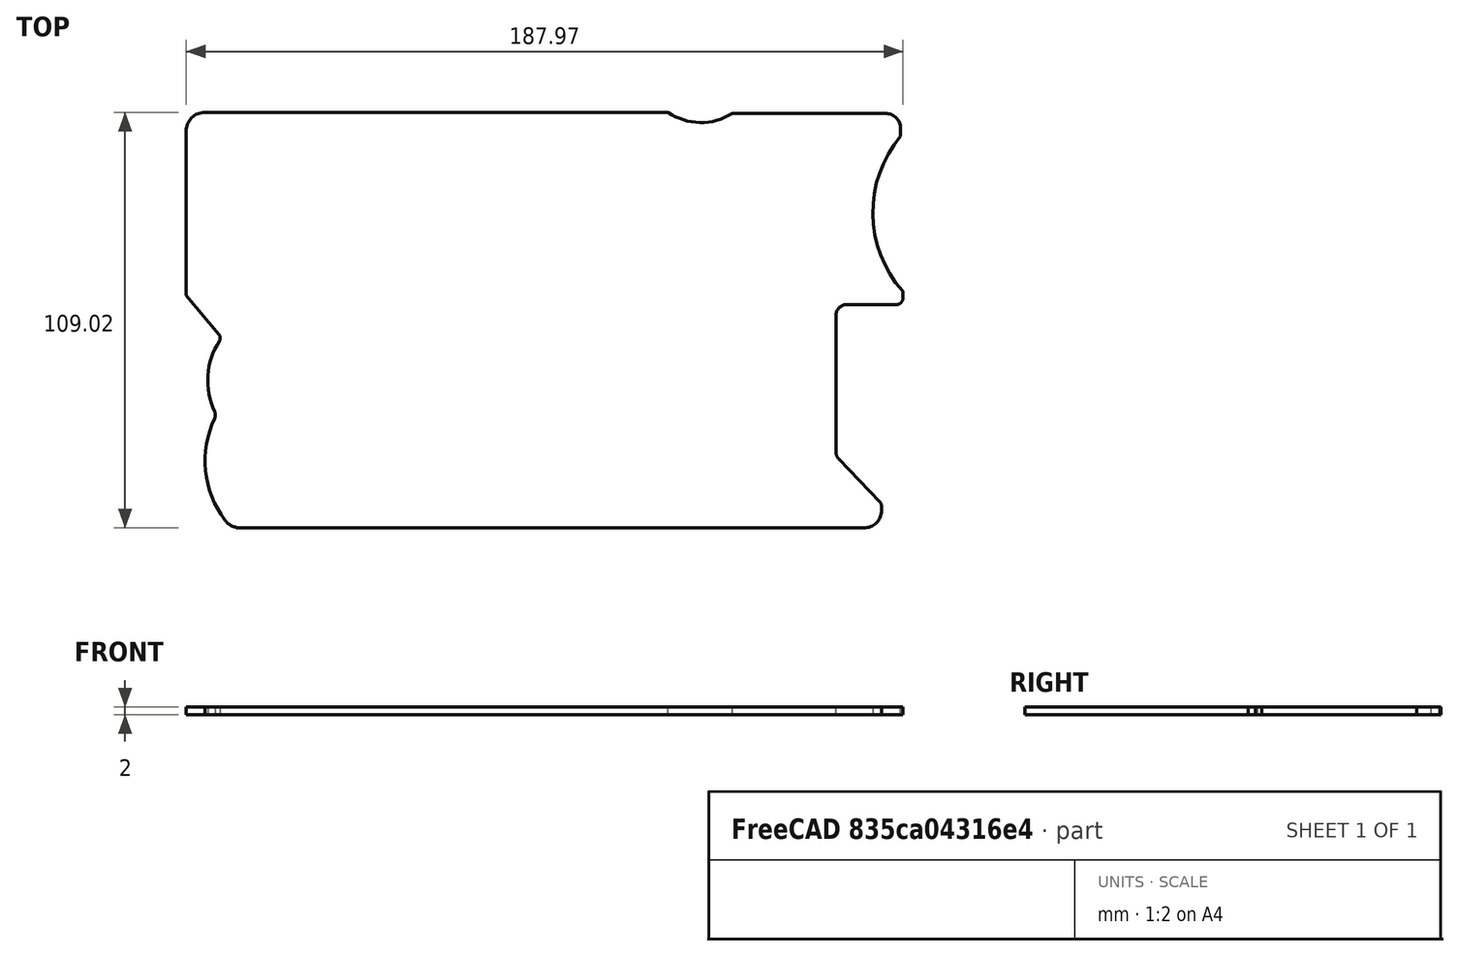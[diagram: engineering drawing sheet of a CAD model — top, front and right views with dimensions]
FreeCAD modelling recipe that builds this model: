
FCSTD DOCUMENT  (FreeCAD 0.20R29177 (Git))
Label: PCB design shape
License: All rights reserved
LicenseURL: http://en.wikipedia.org/wiki/All_rights_reserved
objects: Mesh::Feature×3, Sketcher::SketchObject×2, PartDesign::Body×2, PartDesign::Pad×1, PartDesign::FeatureBase×1
note: 7 computed .brp shape members not serialized (recipe doc carries the construction recipe); baked Part::Feature solids carry a one-line shape summary decoded from their .brp

FEATURE [Mesh::Feature] Base
FEATURE [Mesh::Feature] Cover
  Placement = pos=(0,0,91) rot=(0,0,1;0rad)
FEATURE [Mesh::Feature] Letters
  Placement = pos=(250,0,15) rot=(0,0,1;0rad)
FEATURE [Sketcher::SketchObject] Sketch
  FullyConstrained = false
  MapMode = 5
  Support = -> [XY_Plane]
  sketch-geometry (25):
    g0: LineSegment StartX=410.984 StartY=54.7283 StartZ=0 EndX=532.426 EndY=54.7283 EndZ=0
    g1: LineSegment StartX=593.446 StartY=50.4504 StartZ=0 EndX=593.446 EndY=48.4179 EndZ=0
    g2: LineSegment StartX=583.804 StartY=-54.2856 StartZ=0 EndX=420.385 EndY=-54.2856 EndZ=0
    g3: LineSegment StartX=406.097 StartY=6.73396 StartZ=0 EndX=406.097 EndY=49.8407 EndZ=0
    g4: ArcOfCircle CenterX=541.082 CenterY=67.307 CenterZ=0 NormalX=0 NormalY=0 NormalZ=1 AngleXU=0 Radius=15.2692 StartAngle=4.10966 EndAngle=5.28376
    g5: ArcOfCircle CenterX=617.189 CenterY=28.4278 CenterZ=0 NormalX=0 NormalY=0 NormalZ=1 AngleXU=0 Radius=31.0375 StartAngle=2.44179 EndAngle=3.86807
    g6: LineSegment StartX=579.288 StartY=4.28428 StartZ=0 EndX=592.266 EndY=4.28428 EndZ=0
    g7: LineSegment StartX=576.473 StartY=-34.3297 StartZ=0 EndX=576.473 EndY=1.46836 EndZ=0
    g8: LineSegment StartX=577.24 StartY=-36.2436 StartZ=0 EndX=587.951 EndY=-47.4535 EndZ=0
    g9: LineSegment StartX=588.479 StartY=-48.8004 StartZ=0 EndX=588.466 EndY=-49.6909 EndZ=0
    g10: LineSegment StartX=406.097 StartY=6.73396 StartZ=0 EndX=414.682 EndY=-3.55576 EndZ=0
    g11: ArcOfCircle CenterX=430.76 CenterY=-15.6382 CenterZ=0 NormalX=0 NormalY=0 NormalZ=1 AngleXU=0 Radius=19.0343 StartAngle=2.56663 EndAngle=3.58067
    g12: ArcOfCircle CenterX=437.062 CenterY=-36.6652 CenterZ=0 NormalX=0 NormalY=0 NormalZ=1 AngleXU=0 Radius=26.0034 StartAngle=2.70203 EndAngle=3.78081
    g13: ArcOfCircle CenterX=589.433 CenterY=50.4504 CenterZ=0 NormalX=0 NormalY=0 NormalZ=1 AngleXU=0 Radius=4.01265 StartAngle=-9e-16 EndAngle=1.56794
    g14: ArcOfCircle CenterX=592.266 CenterY=6.08736 CenterZ=0 NormalX=0 NormalY=0 NormalZ=1 AngleXU=0 Radius=1.80308 StartAngle=4.71239 EndAngle=6.28362
    g15: LineSegment StartX=593.987 StartY=7.8114 StartZ=0 EndX=594.069 EndY=6.08814 EndZ=0
    g16: LineSegment StartX=549.34 StartY=54.4631 StartZ=0 EndX=589.445 EndY=54.4631 EndZ=0
    g17: ArcOfCircle CenterX=579.288 CenterY=1.46836 CenterZ=0 NormalX=0 NormalY=0 NormalZ=1 AngleXU=0 Radius=2.81593 StartAngle=1.5708 EndAngle=3.14159
    g18: ArcOfCircle CenterX=583.804 CenterY=-49.623 CenterZ=0 NormalX=0 NormalY=0 NormalZ=1 AngleXU=0 Radius=4.66258 StartAngle=4.71239 EndAngle=6.26864
    g19: ArcOfCircle CenterX=586.57 CenterY=-48.7726 CenterZ=0 NormalX=0 NormalY=0 NormalZ=1 AngleXU=0 Radius=1.90944 StartAngle=6.26864 EndAngle=7.04582
    g20: ArcOfCircle CenterX=420.385 CenterY=-49.0616 CenterZ=0 NormalX=0 NormalY=0 NormalZ=1 AngleXU=0 Radius=5.22406 StartAngle=3.78081 EndAngle=4.71239
    g21: ArcOfCircle CenterX=413.559 CenterY=-4.49227 CenterZ=0 NormalX=0 NormalY=0 NormalZ=1 AngleXU=0 Radius=1.46186 StartAngle=5.70822 EndAngle=6.9785
    g22: ArcOfCircle CenterX=411.541 CenterY=-24.6643 CenterZ=0 NormalX=0 NormalY=0 NormalZ=1 AngleXU=0 Radius=2.19816 StartAngle=5.84362 EndAngle=6.72227
    g23: ArcOfCircle CenterX=579.243 CenterY=-34.3297 CenterZ=0 NormalX=0 NormalY=0 NormalZ=1 AngleXU=0 Radius=2.7704 StartAngle=3.14159 EndAngle=3.90422
    g24: ArcOfCircle CenterX=410.984 CenterY=49.8407 CenterZ=0 NormalX=0 NormalY=0 NormalZ=1 AngleXU=0 Radius=4.88762 StartAngle=1.5708 EndAngle=3.14159
  constraints (32):
    c: Horizontal(g0)
    c: Horizontal(g2)
    c: Vertical(g1)
    c: Vertical(g3)
    c: Horizontal(g6)
    c: Vertical(g7)
    c: Coincident(g16,g13) = 1.5708
    c: Tangent(g1,g13) = 1.5708
    c: Coincident(g15,g14) = 1.5708
    c: Tangent(g6,g14) = -1.5708
    c: Coincident(g1,g5)
    c: Coincident(g15,g5)
    c: Coincident(g0,g4)
    c: Coincident(g16,g4)
    c: Coincident(g3,g10)
    c: Tangent(g6,g17) = 1.5708
    c: Tangent(g7,g17) = 1.5708
    c: Tangent(g2,g18) = 1.5708
    c: Tangent(g9,g18) = 1.5708
    c: Tangent(g8,g19) = 1.5708
    c: Tangent(g9,g19) = 1.5708
    c: Tangent(g2,g20) = 1.5708
    c: Tangent(g12,g20) = -1.5708
    c: Tangent(g10,g21) = 1.5708
    c: Tangent(g11,g21) = 1.5708
    c: Tangent(g11,g22) = 1.5708
    c: Tangent(g12,g22) = 1.5708
    c: Tangent(g8,g23) = -1.5708
    c: Tangent(g7,g23) = 1.5708
    c: Tangent(g0,g24) = 1.5708
    c: Tangent(g3,g24) = 1.5708
    c: Horizontal(g16)
FEATURE [PartDesign::Pad] Pad
  Direction = (0,0,1)
  Length = 2
  Length2 = 10
  Profile = -> Sketch
  ReferenceAxis = -> Sketch [N_Axis]
  Refine = true
  Type = 0
FEATURE [PartDesign::Body] Body  label="PCB"
  Group = -> [Sketch,Pad]
  Origin = -> Origin
  Tip = -> Pad
FEATURE [PartDesign::Body] Body002
  Origin = -> Origin002
FEATURE [PartDesign::FeatureBase] BaseFeature
FEATURE [Sketcher::SketchObject] Sketch001  label="SketchLetters"
  FullyConstrained = false
  MapMode = 5
  sketch-geometry (139):
    g0: LineSegment StartX=405.546 StartY=54.2279 StartZ=0 EndX=416.615 EndY=54.2279 EndZ=0
    g1: LineSegment StartX=422.952 StartY=31.0582 StartZ=0 EndX=416.615 EndY=54.2279 EndZ=0
    g2: LineSegment StartX=422.952 StartY=54.1639 StartZ=0 EndX=422.952 EndY=31.0582 EndZ=0
    g3: LineSegment StartX=431.208 StartY=54.0359 StartZ=0 EndX=422.952 EndY=54.1639 EndZ=0
    g4: LineSegment StartX=431.208 StartY=3.85615 StartZ=0 EndX=431.208 EndY=54.0359 EndZ=0
    g5: LineSegment StartX=421.992 StartY=3.85615 StartZ=0 EndX=431.208 EndY=3.85615 EndZ=0
    g6: LineSegment StartX=414.055 StartY=33.2983 StartZ=0 EndX=421.992 EndY=3.85615 EndZ=0
    g7: LineSegment StartX=414.055 StartY=3.85615 StartZ=0 EndX=414.055 EndY=33.2983 EndZ=0
    g8: LineSegment StartX=405.546 StartY=3.81092 StartZ=0 EndX=414.055 EndY=3.85615 EndZ=0
    g9: LineSegment StartX=405.546 StartY=54.2279 StartZ=0 EndX=405.546 EndY=3.81092 EndZ=0
    g10: GeomPoint X=438.871 Y=54.184 Z=0
    g11: GeomPoint X=461.31 Y=54.184 Z=0
    g12: GeomPoint X=461.31 Y=45.5904 Z=0
    g13: LineSegment StartX=438.871 StartY=54.184 StartZ=0 EndX=461.31 EndY=54.184 EndZ=0
    g14: LineSegment StartX=461.31 StartY=45.5904 StartZ=0 EndX=461.31 EndY=54.184 EndZ=0
    g15: LineSegment StartX=438.871 StartY=54.184 StartZ=0 EndX=438.871 EndY=3.87505 EndZ=0
    g16: LineSegment StartX=461.184 StartY=3.87505 StartZ=0 EndX=438.871 EndY=3.87505 EndZ=0
    g17: LineSegment StartX=461.184 StartY=12.5525 StartZ=0 EndX=461.184 EndY=3.87505 EndZ=0
    g18: LineSegment StartX=461.184 StartY=12.5525 StartZ=0 EndX=448.129 EndY=12.5525 EndZ=0
    g19: LineSegment StartX=448.129 StartY=12.5525 StartZ=0 EndX=448.129 EndY=25.686 EndZ=0
    g20: LineSegment StartX=448.129 StartY=25.686 StartZ=0 EndX=458.682 EndY=25.686 EndZ=0
    g21: LineSegment StartX=458.682 StartY=34.5198 StartZ=0 EndX=458.682 EndY=25.686 EndZ=0
    g22: LineSegment StartX=458.682 StartY=34.5198 StartZ=0 EndX=448.135 EndY=34.5198 EndZ=0
    g23: LineSegment StartX=448.135 StartY=34.5198 StartZ=0 EndX=448.135 EndY=45.5904 EndZ=0
    g24: LineSegment StartX=461.31 StartY=45.5904 StartZ=0 EndX=448.135 EndY=45.5904 EndZ=0
    g25: LineSegment StartX=465.562 StartY=53.9856 StartZ=0 EndX=465.562 EndY=45.5426 EndZ=0
    g26: LineSegment StartX=473.536 StartY=45.5426 StartZ=0 EndX=465.562 EndY=45.5426 EndZ=0
    g27: LineSegment StartX=473.536 StartY=3.7187 StartZ=0 EndX=473.536 EndY=45.5426 EndZ=0
    g28: LineSegment StartX=482.76 StartY=3.7187 StartZ=0 EndX=473.536 EndY=3.7187 EndZ=0
    g29: LineSegment StartX=482.76 StartY=3.7187 StartZ=0 EndX=482.76 EndY=45.5426 EndZ=0
    g30: LineSegment StartX=490.969 StartY=45.5426 StartZ=0 EndX=482.76 EndY=45.5426 EndZ=0
    g31: LineSegment StartX=490.969 StartY=45.5426 StartZ=0 EndX=490.969 EndY=53.9856 EndZ=0
    g32: LineSegment StartX=490.969 StartY=53.9856 StartZ=0 EndX=465.562 EndY=53.9856 EndZ=0
    g33: LineSegment StartX=496.41 StartY=54.2073 StartZ=0 EndX=496.41 EndY=3.71827 EndZ=0
    g34: LineSegment StartX=496.41 StartY=3.71827 StartZ=0 EndX=505.869 EndY=3.71827 EndZ=0
    g35: LineSegment StartX=505.869 StartY=3.71827 StartZ=0 EndX=505.869 EndY=25.0602 EndZ=0
    g36: LineSegment StartX=505.869 StartY=25.0602 StartZ=0 EndX=515.484 EndY=25.0602 EndZ=0
    g37: LineSegment StartX=515.484 StartY=25.0602 StartZ=0 EndX=515.484 EndY=33.7377 EndZ=0
    g38: LineSegment StartX=515.484 StartY=33.7377 StartZ=0 EndX=505.791 EndY=33.7377 EndZ=0
    g39: LineSegment StartX=505.791 StartY=33.7377 StartZ=0 EndX=505.791 EndY=45.5422 EndZ=0
    g40: LineSegment StartX=505.791 StartY=45.5422 StartZ=0 EndX=518.299 EndY=45.5422 EndZ=0
    g41: LineSegment StartX=518.299 StartY=45.5422 StartZ=0 EndX=518.299 EndY=54.2073 EndZ=0
    g42: LineSegment StartX=518.299 StartY=54.2073 StartZ=0 EndX=496.41 EndY=54.2073 EndZ=0
    g43: LineSegment StartX=523.843 StartY=54.2108 StartZ=0 EndX=523.843 EndY=3.71104 EndZ=0
    g44: LineSegment StartX=545.605 StartY=3.71104 StartZ=0 EndX=523.843 EndY=3.71104 EndZ=0
    g45: LineSegment StartX=545.605 StartY=3.71104 StartZ=0 EndX=545.605 EndY=12.5437 EndZ=0
    g46: LineSegment StartX=545.605 StartY=12.5437 StartZ=0 EndX=532.996 EndY=12.5437 EndZ=0
    g47: LineSegment StartX=532.996 StartY=12.5437 StartZ=0 EndX=532.996 EndY=54.2108 EndZ=0
    g48: LineSegment StartX=532.996 StartY=54.2108 StartZ=0 EndX=523.843 EndY=54.2108 EndZ=0
    g49: LineSegment StartX=551.266 StartY=54.0824 StartZ=0 EndX=551.266 EndY=3.77469 EndZ=0
    g50: LineSegment StartX=560.354 StartY=3.77469 StartZ=0 EndX=551.266 EndY=3.77469 EndZ=0
    g51: LineSegment StartX=560.354 StartY=3.77469 StartZ=0 EndX=560.354 EndY=54.0824 EndZ=0
    g52: LineSegment StartX=560.354 StartY=54.0824 StartZ=0 EndX=551.266 EndY=54.0824 EndZ=0
    g53: LineSegment StartX=566.179 StartY=54.1464 StartZ=0 EndX=574.896 EndY=29.6968 EndZ=0
    g54: LineSegment StartX=594.341 StartY=54.2104 StartZ=0 EndX=585.585 EndY=29.5688 EndZ=0
    g55: LineSegment StartX=565.731 StartY=3.9027 StartZ=0 EndX=574.896 EndY=29.6968 EndZ=0
    g56: LineSegment StartX=575.78 StartY=54.1464 StartZ=0 EndX=580.593 EndY=40.4496 EndZ=0
    g57: LineSegment StartX=565.731 StartY=3.9027 StartZ=0 EndX=574.563 EndY=3.9027 EndZ=0
    g58: LineSegment StartX=584.996 StartY=3.77469 StartZ=0 EndX=594.725 EndY=3.77469 EndZ=0
    g59: LineSegment StartX=594.341 StartY=54.2104 StartZ=0 EndX=585.508 EndY=54.2104 EndZ=0
    g60: LineSegment StartX=575.78 StartY=54.1464 StartZ=0 EndX=566.179 EndY=54.1464 EndZ=0
    g61: LineSegment StartX=580.593 StartY=40.4496 StartZ=0 EndX=585.508 EndY=54.2104 EndZ=0
    g62: LineSegment StartX=585.585 StartY=29.5688 StartZ=0 EndX=594.725 EndY=3.77469 EndZ=0
    g63: LineSegment StartX=579.825 StartY=18.816 StartZ=0 EndX=584.996 EndY=3.77469 EndZ=0
    g64: LineSegment StartX=579.825 StartY=18.816 StartZ=0 EndX=574.563 EndY=3.9027 EndZ=0
    g65: LineSegment StartX=565.988 StartY=-3.25487 StartZ=0 EndX=575.396 EndY=-3.25487 EndZ=0
    g66: LineSegment StartX=575.396 StartY=-3.25487 StartZ=0 EndX=575.396 EndY=-44.7299 EndZ=0
    g67: LineSegment StartX=575.396 StartY=-44.7299 StartZ=0 EndX=588.005 EndY=-44.7299 EndZ=0
    g68: LineSegment StartX=588.005 StartY=-44.7299 StartZ=0 EndX=588.005 EndY=-53.5626 EndZ=0
    g69: LineSegment StartX=588.005 StartY=-53.5626 StartZ=0 EndX=565.988 EndY=-53.5626 EndZ=0
    g70: LineSegment StartX=565.988 StartY=-53.5626 StartZ=0 EndX=565.988 EndY=-3.25487 EndZ=0
    g71: LineSegment StartX=538.722 StartY=-3.31887 StartZ=0 EndX=538.722 EndY=-53.5626 EndZ=0
    g72: LineSegment StartX=538.722 StartY=-53.5626 StartZ=0 EndX=560.739 EndY=-53.5626 EndZ=0
    g73: LineSegment StartX=560.739 StartY=-53.5626 StartZ=0 EndX=560.739 EndY=-45.05 EndZ=0
    g74: LineSegment StartX=560.739 StartY=-45.05 StartZ=0 EndX=547.874 EndY=-45.05 EndZ=0
    g75: LineSegment StartX=547.874 StartY=-45.05 StartZ=0 EndX=547.874 EndY=-3.31887 EndZ=0
    g76: LineSegment StartX=547.874 StartY=-3.31887 StartZ=0 EndX=538.722 EndY=-3.31887 EndZ=0
    g77: LineSegment StartX=521.859 StartY=-3.32229 StartZ=0 EndX=521.859 EndY=-53.374 EndZ=0
    g78: LineSegment StartX=521.859 StartY=-53.374 StartZ=0 EndX=531.075 EndY=-53.374 EndZ=0
    g79: LineSegment StartX=531.075 StartY=-53.374 StartZ=0 EndX=531.075 EndY=-3.32229 EndZ=0
    g80: LineSegment StartX=531.075 StartY=-3.32229 StartZ=0 EndX=521.859 EndY=-3.32229 EndZ=0
    g81: LineSegment StartX=489.144 StartY=-3.19528 StartZ=0 EndX=489.144 EndY=-53.503 EndZ=0
    g82: LineSegment StartX=489.144 StartY=-53.503 StartZ=0 EndX=498.361 EndY=-53.503 EndZ=0
    g83: LineSegment StartX=498.361 StartY=-53.503 StartZ=0 EndX=498.361 EndY=-31.7414 EndZ=0
    g84: LineSegment StartX=498.361 StartY=-31.7414 StartZ=0 EndX=504.953 EndY=-31.7414 EndZ=0
    g85: LineSegment StartX=504.953 StartY=-31.7414 StartZ=0 EndX=504.953 EndY=-53.439 EndZ=0
    g86: LineSegment StartX=504.953 StartY=-53.439 StartZ=0 EndX=514.17 EndY=-53.439 EndZ=0
    g87: LineSegment StartX=514.17 StartY=-53.439 StartZ=0 EndX=514.17 EndY=-3.13127 EndZ=0
    g88: LineSegment StartX=514.17 StartY=-3.13127 StartZ=0 EndX=504.953 EndY=-3.13127 EndZ=0
    g89: LineSegment StartX=504.953 StartY=-3.13127 StartZ=0 EndX=504.953 EndY=-23.0367 EndZ=0
    g90: LineSegment StartX=504.953 StartY=-23.0367 StartZ=0 EndX=498.297 EndY=-23.0367 EndZ=0
    g91: LineSegment StartX=498.297 StartY=-23.0367 StartZ=0 EndX=498.297 EndY=-3.13127 EndZ=0
    g92: LineSegment StartX=489.144 StartY=-3.19528 StartZ=0 EndX=498.297 EndY=-3.13127 EndZ=0
    g93: LineSegment StartX=482.961 StartY=-21.1688 StartZ=0 EndX=473.794 EndY=-21.1688 EndZ=0
    g94: LineSegment StartX=473.814 StartY=-33.8649 StartZ=0 EndX=482.541 EndY=-33.8649 EndZ=0
    g95: LineSegment StartX=467.941 StartY=-14.0958 StartZ=0 EndX=467.941 EndY=-43.2309 EndZ=0
    g96: LineSegment StartX=473.814 StartY=-42.8558 StartZ=0 EndX=473.814 EndY=-33.8649 EndZ=0
    g97: LineSegment StartX=473.794 StartY=-21.1688 StartZ=0 EndX=473.794 EndY=-13.9212 EndZ=0
    g98: LineSegment StartX=458.751 StartY=-13.0789 StartZ=0 EndX=458.751 EndY=-44.5006 EndZ=0
    g99: LineSegment StartX=482.541 StartY=-33.8649 StartZ=0 EndX=482.541 EndY=-45.2303 EndZ=0
    g100: LineSegment StartX=482.961 StartY=-21.1688 StartZ=0 EndX=482.961 EndY=-13.405 EndZ=0
    g101: ArcOfCircle CenterX=470.871 CenterY=-14.1044 CenterZ=0 NormalX=0 NormalY=0 NormalZ=1 AngleXU=0 Radius=2.92925 StartAngle=0.0625575 EndAngle=3.13866
    g102: ArcOfCircle CenterX=470.84 CenterY=-14.4077 CenterZ=0 NormalX=0 NormalY=0 NormalZ=1 AngleXU=0 Radius=12.1622 StartAngle=0.0825419 EndAngle=3.03211
    g103: ArcOfCircle CenterX=470.854 CenterY=-42.6787 CenterZ=0 NormalX=0 NormalY=0 NormalZ=1 AngleXU=0 Radius=2.96468 StartAngle=3.32895 EndAngle=6.22339
    g104: ArcOfCircle CenterX=470.729 CenterY=-42.1506 CenterZ=0 NormalX=0 NormalY=0 NormalZ=1 AngleXU=0 Radius=12.2064 StartAngle=3.33532 EndAngle=6.02812
    g105: LineSegment StartX=421.459 StartY=-3.29966 StartZ=0 EndX=433.493 EndY=-3.29966 EndZ=0
    g106: LineSegment StartX=436.191 StartY=-17.5919 StartZ=0 EndX=436.191 EndY=-23.0973 EndZ=0
    g107: LineSegment StartX=420.596 StartY=-54.239 StartZ=0 EndX=419.544 EndY=-54.239 EndZ=0
    g108: LineSegment StartX=411.513 StartY=-46.657 StartZ=0 EndX=411.513 EndY=-34.1508 EndZ=0
    g109: LineSegment StartX=438.418 StartY=-23.0973 StartZ=0 EndX=436.191 EndY=-23.0973 EndZ=0
    g110: LineSegment StartX=423.276 StartY=-31.8053 StartZ=0 EndX=426.847 EndY=-31.8053 EndZ=0
    g111: LineSegment StartX=438.418 StartY=-31.6875 StartZ=0 EndX=438.418 EndY=-23.0973 EndZ=0
    g112: LineSegment StartX=426.879 StartY=-17.5919 StartZ=0 EndX=436.191 EndY=-17.5919 EndZ=0
    g113: LineSegment StartX=436.191 StartY=-17.5919 StartZ=0 EndX=436.191 EndY=-23.0973 EndZ=0
    g114: LineSegment StartX=426.847 StartY=-42.5663 StartZ=0 EndX=426.847 EndY=-31.8053 EndZ=0
    g115: LineSegment StartX=433.535 StartY=-11.8134 StartZ=0 EndX=424.319 EndY=-11.8134 EndZ=0
    g116: LineSegment StartX=421.459 StartY=-3.29966 StartZ=0 EndX=433.535 EndY=-3.29966 EndZ=0
    g117: LineSegment StartX=433.535 StartY=-3.29966 StartZ=0 EndX=433.535 EndY=-11.8134 EndZ=0
    g118: LineSegment StartX=412.104 StartY=-13.7869 StartZ=0 EndX=412.104 EndY=-19.7178 EndZ=0
    g119: LineSegment StartX=421.072 StartY=-20.2759 StartZ=0 EndX=421.072 EndY=-14.1912 EndZ=0
    g120: LineSegment StartX=411.513 StartY=-34.3077 StartZ=0 EndX=411.513 EndY=-42.9125 EndZ=0
    g121: LineSegment StartX=420.95 StartY=-42.8622 StartZ=0 EndX=420.95 EndY=-34.7435 EndZ=0
    g122: ArcOfCircle CenterX=423.743 CenterY=-20.373 CenterZ=0 NormalX=0 NormalY=0 NormalZ=1 AngleXU=0 Radius=2.67256 StartAngle=3.10523 EndAngle=4.61644
    g123: ArcOfCircle CenterX=423.742 CenterY=-14.4315 CenterZ=0 NormalX=0 NormalY=0 NormalZ=1 AngleXU=0 Radius=2.68085 StartAngle=1.35387 EndAngle=3.05183
    g124: ArcOfCircle CenterX=422.511 CenterY=-13.6547 CenterZ=0 NormalX=0 NormalY=0 NormalZ=1 AngleXU=0 Radius=10.4084 StartAngle=1.67205 EndAngle=3.15429
    g125: ArcOfCircle CenterX=424.261 CenterY=-34.9743 CenterZ=0 NormalX=0 NormalY=0 NormalZ=1 AngleXU=0 Radius=3.31845 StartAngle=1.87205 EndAngle=3.07199
    g126: ArcOfCircle CenterX=423.893 CenterY=-42.5966 CenterZ=0 NormalX=0 NormalY=0 NormalZ=1 AngleXU=0 Radius=2.95456 StartAngle=3.23162 EndAngle=6.29341
    g127: ArcOfCircle CenterX=420.07 CenterY=-45.6373 CenterZ=0 NormalX=0 NormalY=0 NormalZ=1 AngleXU=0 Radius=8.61771 StartAngle=3.2602 EndAngle=4.77347
    g128: LineSegment StartX=436.159 StartY=-31.6875 StartZ=0 EndX=438.418 EndY=-31.6875 EndZ=0
    g129: LineSegment StartX=426.879 StartY=-23.0333 StartZ=0 EndX=426.879 EndY=-17.5919 EndZ=0
    g130: LineSegment StartX=426.879 StartY=-23.0333 StartZ=0 EndX=423.487 EndY=-23.0333 EndZ=0
    g131: LineSegment StartX=436.159 StartY=-31.6875 StartZ=0 EndX=436.159 EndY=-50.1365 EndZ=0
    g132: ArcOfCircle CenterX=420.041 CenterY=-20.028 CenterZ=0 NormalX=0 NormalY=0 NormalZ=1 AngleXU=0 Radius=7.9434 StartAngle=3.10253 EndAngle=4.21528
    g133: ArcOfCircle CenterX=419.38 CenterY=-34.2293 CenterZ=0 NormalX=0 NormalY=0 NormalZ=1 AngleXU=0 Radius=7.86764 StartAngle=1.9796 EndAngle=3.15156
    g134: LineSegment StartX=412.104 StartY=-19.7178 StartZ=0 EndX=412.104 EndY=-13.7869 EndZ=0
    g135: LineSegment StartX=427.238 StartY=-51.4102 StartZ=0 EndX=427.883 EndY=-53.5588 EndZ=0
    g136: LineSegment StartX=427.883 StartY=-53.5588 StartZ=0 EndX=437.086 EndY=-53.5588 EndZ=0
    g137: LineSegment StartX=437.086 StartY=-53.5588 StartZ=0 EndX=436.159 EndY=-50.1365 EndZ=0
    g138: ArcOfCircle CenterX=421.114 CenterY=-46.244 CenterZ=0 NormalX=0 NormalY=0 NormalZ=1 AngleXU=0 Radius=8.01171 StartAngle=4.64772 EndAngle=5.58239
  constraints (247):
    c: Horizontal(g0)
    c: Coincident(g1,g0)
    c: Coincident(g2,g1)
    c: Vertical(g2)
    c: Coincident(g3,g2)
    c: Coincident(g4,g3)
    c: Vertical(g4)
    c: Coincident(g5,g4)
    c: Horizontal(g5)
    c: Coincident(g6,g5)
    c: Coincident(g7,g6)
    c: Vertical(g7)
    c: Coincident(g8,g7)
    c: Coincident(g9,g0)
    c: Coincident(g9,g8)
    c: Vertical(g9)
    c: Coincident(g13,g10)
    c: Coincident(g13,g11)
    c: Horizontal(g13)
    c: Coincident(g14,g12)
    c: Coincident(g14,g13)
    c: Vertical(g14)
    c: Coincident(g15,g13)
    c: Vertical(g15)
    c: Coincident(g16,g15)
    c: Horizontal(g16)
    c: Coincident(g17,g16)
    c: Vertical(g17)
    c: Coincident(g18,g17)
    c: Horizontal(g18)
    c: Vertical(g19)
    c: Horizontal(g20)
    c: Coincident(g21,g20)
    c: Vertical(g21)
    c: Coincident(g22,g21)
    c: Horizontal(g22)
    c: Coincident(g23,g22)
    c: Vertical(g23)
    c: Coincident(g24,g14)
    c: Coincident(g24,g23)
    c: Horizontal(g24)
    c: Vertical(g25)
    c: Coincident(g26,g25)
    c: Horizontal(g26)
    c: Coincident(g27,g26)
    c: Vertical(g27)
    c: Coincident(g28,g27)
    c: Horizontal(g28)
    c: Coincident(g29,g28)
    c: Vertical(g29)
    c: Coincident(g30,g29)
    c: Horizontal(g30)
    c: Coincident(g31,g30)
    c: Vertical(g31)
    c: Coincident(g32,g31)
    c: Coincident(g32,g25)
    c: Horizontal(g32)
    c: Vertical(g33)
    c: Horizontal(g34)
    c: Vertical(g35)
    c: Horizontal(g36)
    c: Vertical(g37)
    c: Horizontal(g38)
    c: Vertical(g39)
    c: Coincident(g40,g39)
    c: Horizontal(g40)
    c: Vertical(g41)
    c: Coincident(g42,g33)
    c: Horizontal(g42)
    c: Coincident(g41,g42)
    c: Vertical(g43)
    c: Coincident(g44,g43)
    c: Horizontal(g44)
    c: Coincident(g45,g44)
    c: Vertical(g45)
    c: Coincident(g46,g45)
    c: Horizontal(g46)
    c: Vertical(g47)
    c: Coincident(g48,g43)
    c: Horizontal(g48)
    c: Coincident(g47,g48)
    c: Coincident(g46,g47)
    c: Vertical(g49)
    c: Coincident(g50,g49)
    c: Horizontal(g50)
    c: Coincident(g51,g50)
    c: Vertical(g51)
    c: Coincident(g52,g51)
    c: Coincident(g52,g49)
    c: Horizontal(g52)
    c: Coincident(g57,g55)
    c: Coincident(g57,g64)
    c: Horizontal(g57)
    c: Coincident(g58,g63)
    c: Coincident(g58,g62)
    c: Horizontal(g58)
    c: Coincident(g59,g54)
    c: Coincident(g59,g61)
    c: Horizontal(g59)
    c: Coincident(g60,g56)
    c: Coincident(g60,g53)
    c: Horizontal(g60)
    c: Coincident(g56,g61)
    c: Coincident(g53,g55)
    c: Coincident(g54,g62)
    c: Coincident(g64,g63)
    c: Horizontal(g65)
    c: Vertical(g66)
    c: Coincident(g67,g66)
    c: Horizontal(g67)
    c: Coincident(g68,g67)
    c: Vertical(g68)
    c: Horizontal(g69)
    c: Coincident(g70,g65)
    c: Vertical(g70)
    c: Coincident(g65,g66)
    c: Coincident(g68,g69)
    c: Vertical(g71)
    c: Coincident(g72,g71)
    c: Horizontal(g72)
    c: Coincident(g73,g72)
    c: Vertical(g73)
    c: Coincident(g74,g73)
    c: Horizontal(g74)
    c: Coincident(g75,g74)
    c: Vertical(g75)
    c: Coincident(g76,g75)
    c: Coincident(g76,g71)
    c: Horizontal(g76)
    c: Vertical(g77)
    c: Coincident(g78,g77)
    c: Horizontal(g78)
    c: Coincident(g79,g78)
    c: Vertical(g79)
    c: Coincident(g80,g79)
    c: Coincident(g80,g77)
    c: Horizontal(g80)
    c: Vertical(g81)
    c: Coincident(g82,g81)
    c: Horizontal(g82)
    c: Coincident(g83,g82)
    c: Vertical(g83)
    c: Coincident(g84,g83)
    c: Horizontal(g84)
    c: Coincident(g85,g84)
    c: Vertical(g85)
    c: Coincident(g86,g85)
    c: Horizontal(g86)
    c: Coincident(g87,g86)
    c: Vertical(g87)
    c: Coincident(g88,g87)
    c: Horizontal(g88)
    c: Coincident(g89,g88)
    c: Vertical(g89)
    c: Coincident(g90,g89)
    c: Horizontal(g90)
    c: Coincident(g91,g90)
    c: Vertical(g91)
    c: Coincident(g92,g81)
    c: Coincident(g92,g91)
    c: Horizontal(g93)
    c: Horizontal(g94)
    c: Vertical(g95)
    c: Coincident(g96,g94)
    c: Coincident(g97,g93)
    c: Vertical(g97)
    c: Vertical(g96)
    c: Vertical(g98)
    c: Coincident(g99,g94)
    c: Vertical(g99)
    c: Coincident(g100,g93)
    c: Vertical(g100)
    c: Coincident(g101,g97)
    c: Coincident(g95,g101)
    c: Coincident(g102,g98)
    c: Coincident(g102,g100)
    c: Coincident(g103,g96)
    c: Coincident(g103,g95)
    c: Coincident(g104,g99)
    c: Coincident(g104,g98)
    c: Horizontal(g105)
    c: Horizontal(g107)
    c: Vertical(g106)
    c: Vertical(g108)
    c: Coincident(g128,g111)
    c: Coincident(g111,g109)
    c: Horizontal(g109)
    c: Horizontal(g110)
    c: Vertical(g111)
    c: Coincident(g112,g113)
    c: Coincident(g129,g112)
    c: Horizontal(g112)
    c: Vertical(g113)
    c: Vertical(g114)
    c: Coincident(g116,g117)
    c: Coincident(g117,g115)
    c: Horizontal(g115)
    c: Horizontal(g116)
    c: Vertical(g117)
    c: Vertical(g118)
    c: Vertical(g119)
    c: Vertical(g120)
    c: Vertical(g121)
    c: PointOnObject(g120,g108)
    c: Coincident(g105,g116)
    c: Coincident(g130,g122)
    c: Coincident(g110,g125)
    c: Coincident(g114,g110)
    c: Coincident(g130,g129)
    c: Coincident(g106,g109)
    c: Coincident(g131,g128)
    c: PointOnObject(g106,g112)
    c: Coincident(g105,g124)
    c: Coincident(g134,g118)
    c: Coincident(g134,g124)
    c: Coincident(g108,g127)
    c: PointOnObject(g107,g127)
    c: Coincident(g132,g118)
    c: Coincident(g133,g120)
    c: Coincident(g133,g132)
    c: PointOnObject(g108,g133)
    c: Coincident(g118,g134)
    c: Coincident(g121,g125)
    c: Coincident(g121,g126)
    c: Coincident(g114,g126)
    c: Horizontal(g128)
    c: Coincident(g119,g123)
    c: Coincident(g115,g123)
    c: Coincident(g119,g122)
    c: Coincident(g136,g135)
    c: Horizontal(g136)
    c: Coincident(g137,g136)
    c: Coincident(g131,g137)
    c: Coincident(g107,g127)
    c: Coincident(g138,g135)
    c: Coincident(g138,g107)
    c: Coincident(g19,g20)
    c: Coincident(g18,g19)
    c: Coincident(g40,g41)
    c: Coincident(g38,g39)
    c: Coincident(g37,g38)
    c: Coincident(g36,g37)
    c: Coincident(g35,g36)
    c: Coincident(g33,g34)
    c: Coincident(g34,g35)
    c: Coincident(g69,g70)
    c: Coincident(g106,g113)
